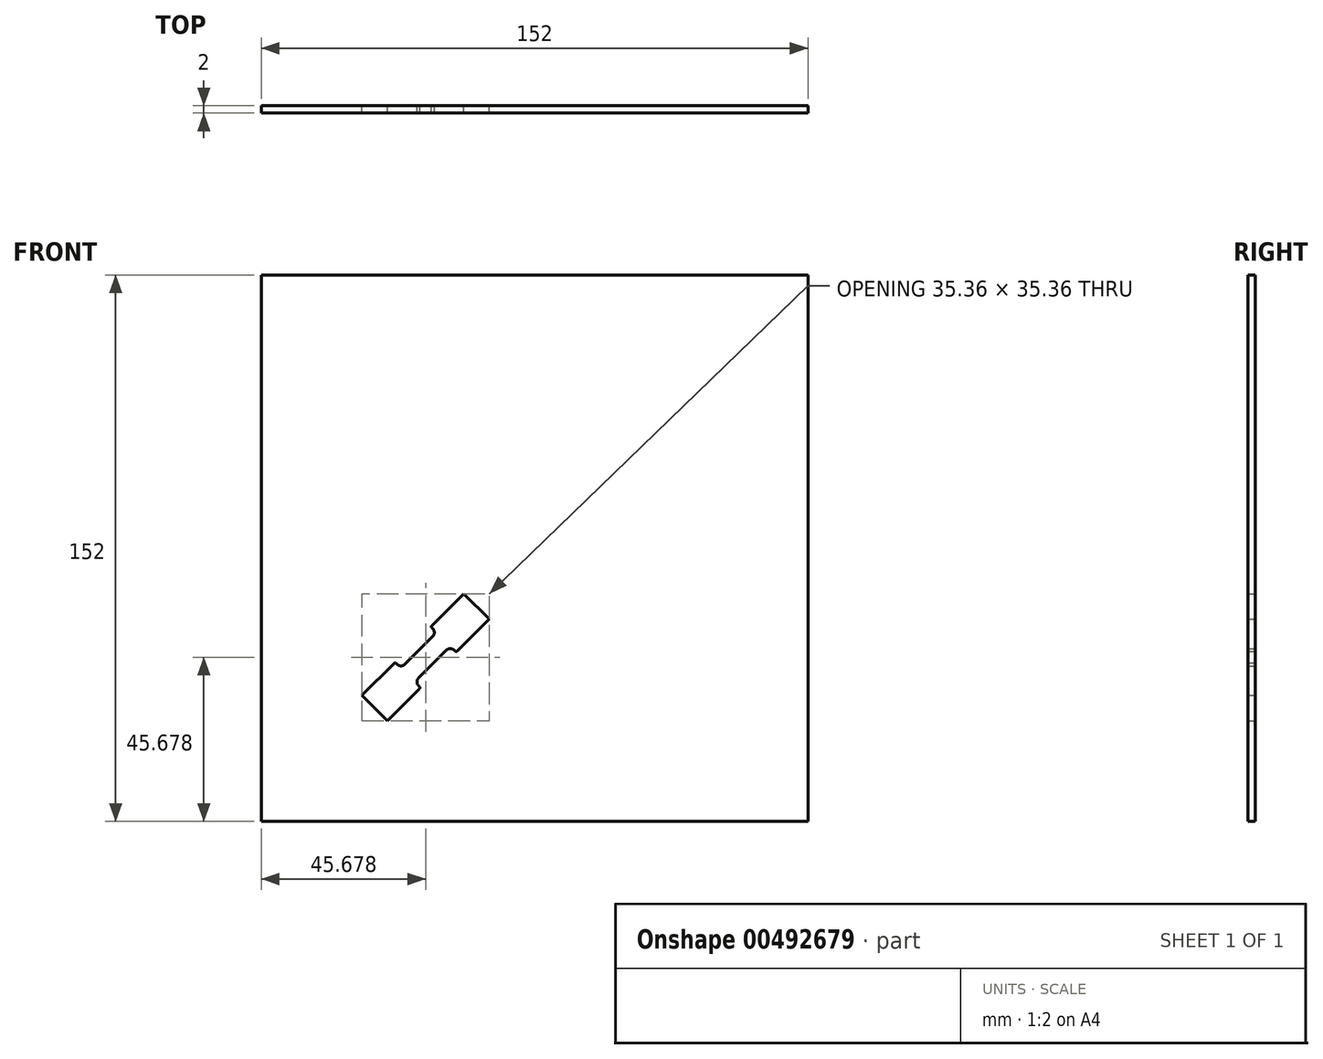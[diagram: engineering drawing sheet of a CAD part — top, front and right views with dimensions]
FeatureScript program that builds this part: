
annotation { "Feature Type Name" : "Feature", "Feature Type Description" : "" }
export const myFeature = defineFeature(function(context is Context, id is Id, definition is map)
    precondition{}
    {
        {
            var Q0;
            Q0=qCreatedBy(makeId("Front.planeOp"),FACE);
            var sketch = newSketch(context, id + "F0", { "sketchPlane" : qUnion([Q0])});
            skLineSegment(sketch, "E0", {"start": v(0, 0) * mm, "end": v(152, 0) * mm});
            skLineSegment(sketch, "E1", {"start": v(152, 0) * mm, "end": v(152, 152) * mm});
            skLineSegment(sketch, "E2", {"start": v(152, 152) * mm, "end": v(0, 152) * mm});
            skLineSegment(sketch, "E3", {"start": v(0, 152) * mm, "end": v(0, 0) * mm});
            skLineSegment(sketch, "E4", {"start": v(35.07, 28) * mm, "end": v(28, 35.07) * mm});
            skLineSegment(sketch, "E5", {"start": v(28, 35.07) * mm, "end": v(36.84, 43.9) * mm});
            skLineSegment(sketch, "E6", {"start": v(35.07, 28) * mm, "end": v(43.9, 36.84) * mm});
            skLineSegment(sketch, "E7", {"start": v(43.9, 37.55) * mm, "end": v(43.7, 37.76) * mm});
            skLineSegment(sketch, "E8", {"start": v(43.7, 39.88) * mm, "end": v(51.48, 47.66) * mm});
            skLineSegment(sketch, "E9", {"start": v(53.6, 47.66) * mm, "end": v(53.8, 47.45) * mm});
            skLineSegment(sketch, "E10", {"start": v(54.52, 47.45) * mm, "end": v(63.36, 56.28) * mm});
            skLineSegment(sketch, "E11", {"start": v(63.36, 56.28) * mm, "end": v(56.28, 63.36) * mm});
            skLineSegment(sketch, "E12", {"start": v(56.28, 63.36) * mm, "end": v(47.45, 54.52) * mm});
            skLineSegment(sketch, "E13", {"start": v(47.45, 53.8) * mm, "end": v(47.66, 53.6) * mm});
            skLineSegment(sketch, "E14", {"start": v(37.55, 43.9) * mm, "end": v(37.76, 43.7) * mm});
            skLineSegment(sketch, "E15", {"start": v(39.88, 43.7) * mm, "end": v(47.66, 51.48) * mm});
            skPoint(sketch, "E16.visualSharp", {"position": v(47.1, 54.16) * mm});
            skArc(sketch, "E16.filletArc", {"start": v(47.45, 54.52) * mm, "mid": v(47.3, 54.16) * mm, "end": v(47.45, 53.8) * mm});
            skPoint(sketch, "E17.visualSharp", {"position": v(54.16, 47.1) * mm});
            skArc(sketch, "E17.filletArc", {"start": v(53.8, 47.45) * mm, "mid": v(54.16, 47.3) * mm, "end": v(54.52, 47.45) * mm});
            skPoint(sketch, "E18.visualSharp", {"position": v(44.26, 37.2) * mm});
            skArc(sketch, "E18.filletArc", {"start": v(43.9, 36.84) * mm, "mid": v(44.06, 37.2) * mm, "end": v(43.9, 37.55) * mm});
            skPoint(sketch, "E19.visualSharp", {"position": v(37.2, 44.26) * mm});
            skArc(sketch, "E19.filletArc", {"start": v(37.55, 43.9) * mm, "mid": v(37.2, 44.06) * mm, "end": v(36.84, 43.9) * mm});
            skPoint(sketch, "E20.visualSharp", {"position": v(48.72, 52.54) * mm});
            skArc(sketch, "E20.filletArc", {"start": v(47.66, 51.48) * mm, "mid": v(48.1, 52.54) * mm, "end": v(47.66, 53.6) * mm});
            skPoint(sketch, "E21.visualSharp", {"position": v(52.54, 48.72) * mm});
            skArc(sketch, "E21.filletArc", {"start": v(53.6, 47.66) * mm, "mid": v(52.54, 48.1) * mm, "end": v(51.48, 47.66) * mm});
            skPoint(sketch, "E22.visualSharp", {"position": v(38.82, 42.64) * mm});
            skArc(sketch, "E22.filletArc", {"start": v(37.76, 43.7) * mm, "mid": v(38.82, 43.26) * mm, "end": v(39.88, 43.7) * mm});
            skPoint(sketch, "E23.visualSharp", {"position": v(42.64, 38.82) * mm});
            skArc(sketch, "E23.filletArc", {"start": v(43.7, 39.88) * mm, "mid": v(43.26, 38.82) * mm, "end": v(43.7, 37.76) * mm});
            skSolve(sketch);
        }
        {
            var Q0;
            Q0=makeQuery(id+"F0.imprint","IMPRINT",FACE,{"disambiguationData":[TD([[makeQuery(id+"F0.imprint","IMPRINT",EDGE,{"derivedFrom":sQuery(id+"F0.wireOp",EDGE,"E0")}),1.0]])]});
            extrude(context, id + "F1", {"entities" : qUnion([Q0]), "depth" : 2 * mm});
        }
        {
            var Q0;
            Q0=makeQuery(id+"F0.imprint","IMPRINT",FACE,{"disambiguationData":[TD([[makeQuery(id+"F0.imprint","IMPRINT",EDGE,{"derivedFrom":sQuery(id+"F0.wireOp",EDGE,"E4")}),-1.0]])]});
            extrude(context, id + "F2", {"entities" : qUnion([Q0]), "operationType" : NewBodyOperationType.REMOVE, "depth" : 2 * mm});
        }
    });
